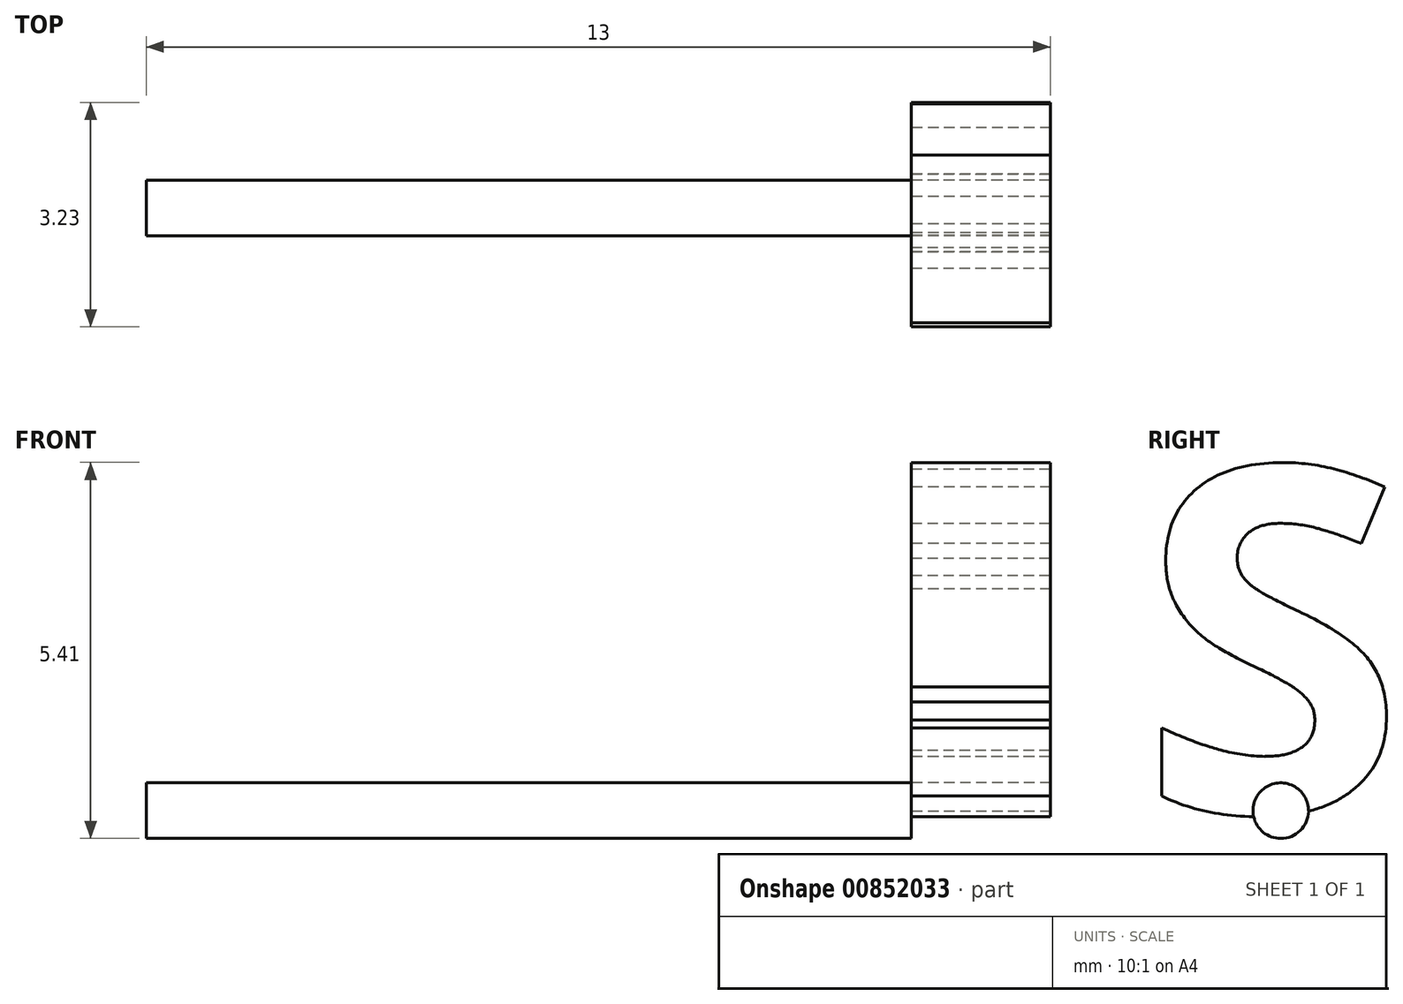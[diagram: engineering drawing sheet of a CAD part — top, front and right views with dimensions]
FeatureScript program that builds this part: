
annotation { "Feature Type Name" : "Feature", "Feature Type Description" : "" }
export const myFeature = defineFeature(function(context is Context, id is Id, definition is map)
    precondition{}
    {
        {
            var Q0;
            Q0=qCreatedBy(makeId("Right.planeOp"),FACE);
            var sketch = newSketch(context, id + "F0", { "sketchPlane" : qUnion([Q0])});
            skCircle(sketch, "E0", {"center": v(0, 0) * mm, "radius": 0.4 * mm});
            skSolve(sketch);
        }
        {
            var Q0;
            Q0 = qSketchRegion(id + "F0", true);
            extrude(context, id + "F1", {"entities" : qUnion([Q0]), "depth" : 11 * mm, "offsetDistance" : 25 * mm});
        }
        {
            var Q0;
            Q0=makeQuery(id+"F1.opExtrude","CAP_FACE",FACE,{"disambiguationData":[OSD([sQuery(id+"F0.wireOp",EDGE,"E0")])],"isStart":false});
            var sketch = newSketch(context, id + "F2", { "sketchPlane" : qUnion([Q0])});
            skText(sketch, "E1", { "text": "S", "fontName": "OpenSans-Bold.ttf"});
            const initialGuessF2  = {"E1": [-0.00203, -2e-05, 1, 0, 0.005]};
            skSetInitialGuess(sketch, initialGuessF2);
            skSolve(sketch);
        }
        {
            var Q0;
            {var subQ5=sQuery(id+"F2.wireOp",EDGE,"E1.sketch_text.stroke-0");Q0=makeQuery(id+"F2.imprint","IMPRINT",FACE,{"disambiguationData":[TD([[makeQuery(id+"F2.imprint","IMPRINT",EDGE,{"derivedFrom":subQ5}),-1.0]])]});}
            extrude(context, id + "F3", {"entities" : qUnion([Q0]), "depth" : 2 * mm, "offsetDistance" : 25 * mm});
        }
    });
